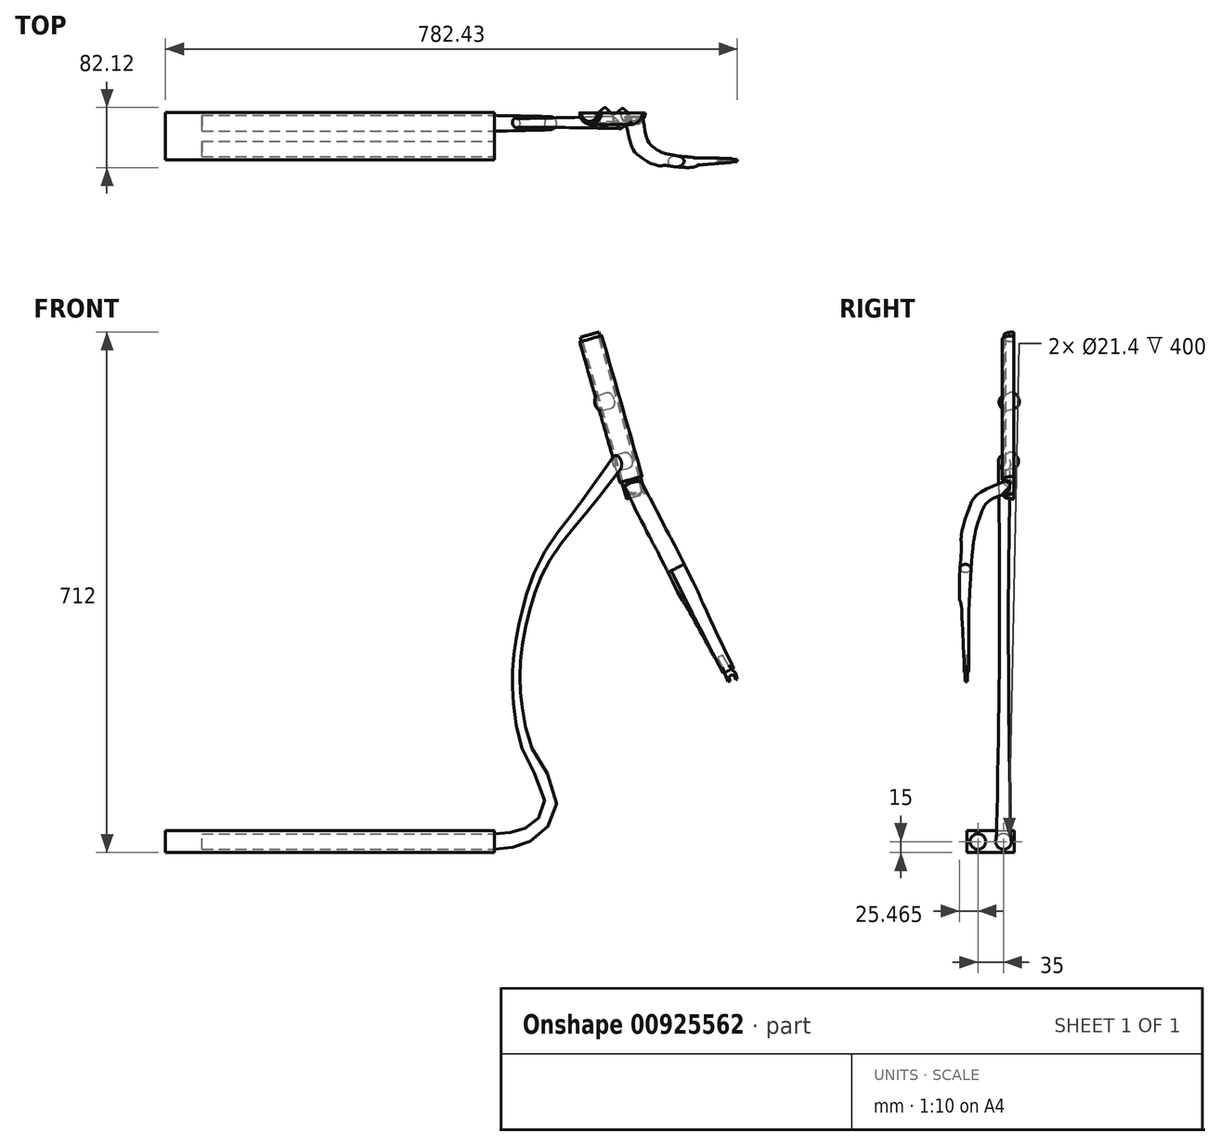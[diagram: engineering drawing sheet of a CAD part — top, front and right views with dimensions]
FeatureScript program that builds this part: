
annotation { "Feature Type Name" : "Feature", "Feature Type Description" : "" }
export const myFeature = defineFeature(function(context is Context, id is Id, definition is map)
    precondition{}
    {
        {
            var Q0;
            Q0=qCreatedBy(makeId("Front.planeOp"),FACE);
            var sketch = newSketch(context, id + "F0", { "sketchPlane" : qUnion([Q0])});
            skLineSegment(sketch, "E0", {"start": v(-867.72, 25) * mm, "end": v(859.87, 25) * mm, "construction": true});
            skLineSegment(sketch, "E1", {"start": v(-316.45, 130) * mm, "end": v(506.8, 130) * mm, "construction": true});
            skLineSegment(sketch, "E2", {"start": v(553.9, -69.15) * mm, "end": v(287, 861.66) * mm, "construction": true});
            skLineSegment(sketch, "E3", {"start": v(-370.15, 525) * mm, "end": v(884.43, 525) * mm, "construction": true});
            skCircle(sketch, "E4", {"center": v(508.78, 298.91) * mm, "radius": 250 * mm, "construction": true});
            skLineSegment(sketch, "E5", {"start": v(508.78, 298.91) * mm, "end": v(455.91, 283.75) * mm, "construction": true});
            skLineSegment(sketch, "E6", {"start": v(508.78, 298.91) * mm, "end": v(371.65, 566.47) * mm, "construction": true});
            skLineSegment(sketch, "E7", {"start": v(-351.72, 690) * mm, "end": v(523.86, 690) * mm, "construction": true});
            skPoint(sketch, "E8", {"position": v(339.42, 690) * mm});
            skLineSegment(sketch, "E9", {"start": v(359.58, 571.29) * mm, "end": v(395.31, 584.53) * mm});
            skLineSegment(sketch, "E10", {"start": v(306.42, 764.88) * mm, "end": v(341.25, 777.78) * mm});
            skCircle(sketch, "E11", {"center": v(-491.22, 301.56) * mm, "radius": 250 * mm, "construction": true});
            skLineSegment(sketch, "E12", {"start": v(-491.22, 301.56) * mm, "end": v(831.47, 298.91) * mm, "construction": true});
            skLineSegment(sketch, "E13.bottom", {"start": v(225, 111.68) * mm, "end": v(-225, 111.68) * mm, "construction": true});
            skLineSegment(sketch, "E13.top", {"start": v(225, -11.68) * mm, "end": v(-225, -11.68) * mm, "construction": true});
            skLineSegment(sketch, "E13.left", {"start": v(225, 111.68) * mm, "end": v(225, -11.68) * mm, "construction": true});
            skLineSegment(sketch, "E13.right", {"start": v(-225, 111.68) * mm, "end": v(-225, -11.68) * mm, "construction": true});
            skPoint(sketch, "E13.middle", {"position": v(0, 50) * mm});
            skLineSegment(sketch, "E14", {"start": v(-491.22, 301.56) * mm, "end": v(-225, 111.68) * mm, "construction": true});
            skLineSegment(sketch, "E15", {"start": v(225, 111.68) * mm, "end": v(220.1, 287.85) * mm, "construction": true});
            skCircle(sketch, "E16", {"center": v(508.78, 298.91) * mm, "radius": 275 * mm});
            skCircle(sketch, "E17", {"center": v(-491.22, 301.56) * mm, "radius": 275 * mm});
            skArc(sketch, "E18", {"start": v(359.58, 571.29) * mm, "mid": v(254.76, 446.83) * mm, "end": v(220.1, 287.85) * mm, "construction": true});
            skSolve(sketch);
        }
        {
            var Q0;
            Q0=qCreatedBy(makeId("Front.planeOp"),FACE);
            var sketch = newSketch(context, id + "F1", { "sketchPlane" : qUnion([Q0])});
            skLineSegment(sketch, "E19", {"start": v(363.24, 558.02) * mm, "end": v(546.56, 610.6) * mm, "construction": true});
            skSolve(sketch);
        }
        {
            var Q0;
            Q0=sQuery(id+"F1.wireOp",EDGE,"E19");
            cPlane(context, id + "F2", {"entities" : qUnion([Q0]), "cplaneType" : CPlaneType.LINE_ANGLE, "offset" : 25 * mm, "angle" : 90 * degree, "width" : 150 * mm, "height" : 150 * mm});
        }
        {
            var Q0;
            Q0=qCreatedBy(id+"F2.planeOp",FACE);
            cPlane(context, id + "F3", {"entities" : qUnion([Q0]), "cplaneType" : CPlaneType.OFFSET, "offset" : 200 * mm, "width" : 150 * mm, "height" : 150 * mm});
        }
        {
            var Q0;
            Q0=qCreatedBy(id+"F2.planeOp",FACE);
            var sketch = newSketch(context, id + "F4", { "sketchPlane" : qUnion([Q0])});
            skCircle(sketch, "E20", {"center": v(502.98, 0) * mm, "radius": 19.15 * mm});
            skSolve(sketch);
        }
        {
            var Q0;
            Q0=qCreatedBy(makeId("Front.planeOp"),FACE);
            var sketch = newSketch(context, id + "F5", { "sketchPlane" : qUnion([Q0])});
            skLineSegment(sketch, "E21", {"start": v(330.52, 767.06) * mm, "end": v(385.68, 574.81) * mm});
            skLineSegment(sketch, "E22.0", {"start": v(329.45, 766.44) * mm, "end": v(384.44, 574.77) * mm});
            skLineSegment(sketch, "E23", {"start": v(329.96, 766.9) * mm, "end": v(330.52, 767.06) * mm});
            skLineSegment(sketch, "E24", {"start": v(385.68, 574.81) * mm, "end": v(385.1, 574.65) * mm});
            skPoint(sketch, "E25.visualSharp", {"position": v(336.55, 759.96) * mm});
            skArc(sketch, "E25.filletArc", {"start": v(336.56, 759.92) * mm, "mid": v(336.54, 759.94) * mm, "end": v(336.51, 759.94) * mm});
            skArc(sketch, "E26.filletArc", {"start": v(382.18, 607.52) * mm, "mid": v(382.2, 607.54) * mm, "end": v(382.2, 607.57) * mm});
            skLineSegment(sketch, "E27", {"start": v(329.45, 766.44) * mm, "end": v(330.05, 766.6) * mm});
            skLineSegment(sketch, "E28", {"start": v(330.05, 766.6) * mm, "end": v(329.96, 766.9) * mm});
            skPoint(sketch, "E29.orphan", {"position": v(335.4, 759.62) * mm});
            skLineSegment(sketch, "E30", {"start": v(384.44, 574.77) * mm, "end": v(385.08, 574.95) * mm});
            skLineSegment(sketch, "E31", {"start": v(385, 574.93) * mm, "end": v(385.1, 574.65) * mm});
            skLineSegment(sketch, "E32", {"start": v(326.59, 772) * mm, "end": v(390, 550.9) * mm});
            skLineSegment(sketch, "E33", {"start": v(390, 550.9) * mm, "end": v(388.16, 550.38) * mm});
            skLineSegment(sketch, "E34", {"start": v(388.16, 550.38) * mm, "end": v(324.75, 771.52) * mm});
            skLineSegment(sketch, "E35", {"start": v(324.75, 771.52) * mm, "end": v(326.59, 772) * mm});
            skSolve(sketch);
        }
        {
            var Q0;
            Q0 = qSketchRegion(id + "F5", true);
            var Q1;
            Q1=sQuery(id+"F0.wireOp",EDGE,"E2");
            revolve(context, id + "F6", {"surfaceOperationType" : NewSurfaceOperationType.NEW, "entities" : qUnion([Q0]), "axis" : qUnion([Q1]), "revolveType" : RevolveType.ONE_DIRECTION, "oppositeDirection" : true, "angle" : 180 * degree});
        }
        {
            var Q0;
            Q0=sQuery(id+"F0.wireOp",EDGE,"E6");
            cPlane(context, id + "F7", {"entities" : qUnion([Q0]), "cplaneType" : CPlaneType.LINE_ANGLE, "offset" : 25 * mm, "angle" : 0 * degree, "width" : 150 * mm, "height" : 150 * mm});
        }
        {
            var Q0;
            Q0=qCreatedBy(id+"F7.planeOp",FACE);
            var sketch = newSketch(context, id + "F8", { "sketchPlane" : qUnion([Q0])});
            skLineSegment(sketch, "E36", {"start": v(0, 33.94) * mm, "end": v(-65, 33.94) * mm, "construction": true});
            skFitSpline(sketch, "E37", {"points": [v(-5.34, 328.4) * mm, v(-52.14, 293.61) * mm, v(-62.93, 251.7) * mm, v(-67.18, 151.52) * mm, v(-65, 44.96) * mm], "startDerivative": vector(-442.33, 23.28) * mm, "endDerivative": vector(3.64, -561.75) * mm});
            skSolve(sketch);
        }
        {
            var Q0;
            Q0=sQuery(id+"F8.wireOp",EDGE,"E36");
            var Q1;
            Q1=sQuery(id+"F8.wireOp",VERTEX,"E36.end");
            cPlane(context, id + "F9", {"entities" : qUnion([Q0, Q1]), "cplaneType" : CPlaneType.CURVE_POINT, "offset" : 25 * mm, "width" : 150 * mm, "height" : 150 * mm});
        }
        {
            var Q0;
            Q0=qCreatedBy(id+"F9.planeOp",FACE);
            var sketch = newSketch(context, id + "F10", { "sketchPlane" : qUnion([Q0])});
            skArc(sketch, "E38.0", {"start": v(512.63, 300.02) * mm, "mid": v(507.68, 302.76) * mm, "end": v(504.94, 297.81) * mm});
            skLineSegment(sketch, "E39.0", {"start": v(505.96, 294.61) * mm, "end": v(504.94, 297.81) * mm});
            skLineSegment(sketch, "E40.0", {"start": v(512.63, 300.02) * mm, "end": v(513.62, 296.52) * mm});
            skLineSegment(sketch, "E41", {"start": v(513.62, 296.52) * mm, "end": v(516, 297.2) * mm});
            skLineSegment(sketch, "E42", {"start": v(516, 297.2) * mm, "end": v(513.62, 304.94) * mm});
            skLineSegment(sketch, "E43", {"start": v(505.96, 294.61) * mm, "end": v(503.18, 293.72) * mm});
            skLineSegment(sketch, "E44", {"start": v(503.18, 293.72) * mm, "end": v(501.9, 297.7) * mm});
            skLineSegment(sketch, "E45", {"start": v(501.9, 297.7) * mm, "end": v(495.51, 313.34) * mm});
            skLineSegment(sketch, "E46", {"start": v(503.46, 316.2) * mm, "end": v(513.62, 304.94) * mm});
            skLineSegment(sketch, "E47", {"start": v(503.46, 316.2) * mm, "end": v(495.95, 329.85) * mm});
            skLineSegment(sketch, "E48", {"start": v(495.95, 329.85) * mm, "end": v(489.19, 326.8) * mm});
            skLineSegment(sketch, "E49", {"start": v(489.19, 326.8) * mm, "end": v(495.51, 313.34) * mm});
            skSolve(sketch);
        }
        {
            var Q0;
            Q0 = qSketchRegion(id + "F10", true);
            extrude(context, id + "F11", {"entities" : qUnion([Q0]), "endBound" : BoundingType.SYMMETRIC, "depth" : 3 * mm, "offsetDistance" : 25 * mm});
        }
        {
            var Q0;
            Q0=sQuery(id+"F8.wireOp",EDGE,"E37");
            var Q1;
            Q1=sQuery(id+"F8.wireOp",VERTEX,"E37.end");
            cPlane(context, id + "F12", {"entities" : qUnion([Q0, Q1]), "cplaneType" : CPlaneType.CURVE_POINT, "offset" : 25 * mm, "width" : 150 * mm, "height" : 150 * mm});
        }
        {
            var Q0;
            Q0=qCreatedBy(id+"F12.planeOp",FACE);
            var sketch = newSketch(context, id + "F13", { "sketchPlane" : qUnion([Q0])});
            skEllipse(sketch, "E50", {"center": v(589.33, 62.75) * mm, "majorRadius": 8 * mm, "minorRadius": 3 * mm, "majorAxis": v(-1, 0)});
            skSolve(sketch);
        }
        {
            var Q0;
            Q0=sQuery(id+"F8.wireOp",VERTEX,"E37.3.internal");
            var Q1;
            Q1=sQuery(id+"F8.wireOp",EDGE,"E37");
            cPlane(context, id + "F14", {"entities" : qUnion([Q0, Q1]), "cplaneType" : CPlaneType.CURVE_POINT, "offset" : 25 * mm, "width" : 150 * mm, "height" : 150 * mm});
        }
        {
            var Q0;
            Q0=sQuery(id+"F8.wireOp",EDGE,"E37");
            cPoint(context, id + "F15", {"entities" : qUnion([Q0]), "parameter" : 0.5});
        }
        {
            var Q0;
            Q0 = qCreatedBy(id + "F15" ,VERTEX);
            var Q1;
            Q1=sQuery(id+"F8.wireOp",EDGE,"E37");
            cPlane(context, id + "F16", {"entities" : qUnion([Q0, Q1]), "cplaneType" : CPlaneType.CURVE_POINT, "offset" : 25 * mm, "width" : 150 * mm, "height" : 150 * mm});
        }
        {
            var Q0;
            Q0=qCreatedBy(id+"F16.planeOp",FACE);
            var sketch = newSketch(context, id + "F17", { "sketchPlane" : qUnion([Q0])});
            skEllipse(sketch, "E51", {"center": v(587.69, 84.2) * mm, "majorRadius": 12.5 * mm, "minorRadius": 7.5 * mm, "majorAxis": v(-1, 0)});
            skSolve(sketch);
        }
        {
            var Q0;
            Q0=sQuery(id+"F8.wireOp",VERTEX,"E37.2.internal");
            var Q1;
            Q1=sQuery(id+"F8.wireOp",EDGE,"E37");
            cPlane(context, id + "F18", {"entities" : qUnion([Q0, Q1]), "cplaneType" : CPlaneType.CURVE_POINT, "offset" : 25 * mm, "width" : 150 * mm, "height" : 150 * mm});
        }
        {
            var Q0;
            Q0=qCreatedBy(id+"F18.planeOp",FACE);
            var sketch = newSketch(context, id + "F19", { "sketchPlane" : qUnion([Q0])});
            skEllipse(sketch, "E52", {"center": v(581.49, 134.07) * mm, "majorRadius": 12.5 * mm, "minorRadius": 9 * mm, "majorAxis": v(-1, 0)});
            skSolve(sketch);
        }
        {
            var Q0;
            Q0=sQuery(id+"F8.wireOp",VERTEX,"E37.1.internal");
            var Q1;
            Q1=sQuery(id+"F8.wireOp",EDGE,"E37");
            cPlane(context, id + "F20", {"entities" : qUnion([Q0, Q1]), "cplaneType" : CPlaneType.CURVE_POINT, "offset" : 25 * mm, "width" : 150 * mm, "height" : 150 * mm});
        }
        {
            var Q0;
            Q0=qCreatedBy(id+"F20.planeOp",FACE);
            var sketch = newSketch(context, id + "F21", { "sketchPlane" : qUnion([Q0])});
            skEllipse(sketch, "E53", {"center": v(553.64, 251.52) * mm, "majorRadius": 12.5 * mm, "minorRadius": 9 * mm, "majorAxis": v(-1, 0)});
            skSolve(sketch);
        }
        {
            var Q0;
            Q0=sQuery(id+"F8.wireOp",VERTEX,"E37.start");
            var Q1;
            Q1=sQuery(id+"F8.wireOp",EDGE,"E37");
            cPlane(context, id + "F22", {"entities" : qUnion([Q0, Q1]), "cplaneType" : CPlaneType.CURVE_POINT, "offset" : 25 * mm, "width" : 150 * mm, "height" : 150 * mm});
        }
        {
            var Q0;
            Q0=qCreatedBy(id+"F22.planeOp",FACE);
            var sketch = newSketch(context, id + "F23", { "sketchPlane" : qUnion([Q0])});
            skEllipse(sketch, "E54", {"center": v(374.92, 560.35) * mm, "majorRadius": 12.5 * mm, "minorRadius": 9 * mm, "majorAxis": v(-1, 0)});
            skSolve(sketch);
        }
        {
            var Q0;
            Q0=sQuery(id+"F8.wireOp",EDGE,"E37");
            var Q2;
            Q2=makeQuery(id+"F13.imprint","IMPRINT",FACE,{"disambiguationData":[TD([[makeQuery(id+"F13.imprint","IMPRINT",EDGE,{"derivedFrom":sQuery(id+"F13.wireOp",EDGE,"E50")}),1.0]])]});
            var Q3;
            Q3=makeQuery(id+"F17.imprint","IMPRINT",FACE,{"disambiguationData":[TD([[makeQuery(id+"F17.imprint","IMPRINT",EDGE,{"derivedFrom":sQuery(id+"F17.wireOp",EDGE,"E51")}),1.0]])]});
            var Q4;
            Q4=makeQuery(id+"F19.imprint","IMPRINT",FACE,{"disambiguationData":[TD([[makeQuery(id+"F19.imprint","IMPRINT",EDGE,{"derivedFrom":sQuery(id+"F19.wireOp",EDGE,"E52")}),1.0]])]});
            var Q5;
            Q5=makeQuery(id+"F21.imprint","IMPRINT",FACE,{"disambiguationData":[TD([[makeQuery(id+"F21.imprint","IMPRINT",EDGE,{"derivedFrom":sQuery(id+"F21.wireOp",EDGE,"E53")}),1.0]])]});
            var Q6;
            Q6=makeQuery(id+"F23.imprint","IMPRINT",FACE,{"disambiguationData":[TD([[makeQuery(id+"F23.imprint","IMPRINT",EDGE,{"derivedFrom":sQuery(id+"F23.wireOp",EDGE,"E54")}),1.0]])]});
            loft(context, id + "F24", {"addSections" : true, "spine" : qUnion([Q0]), "sectionCount" : 5, "sheetProfilesArray" : [{ "sheetProfileEntities" : qUnion([Q2]) }, { "sheetProfileEntities" : qUnion([Q3]) }, { "sheetProfileEntities" : qUnion([Q4]) }, { "sheetProfileEntities" : qUnion([Q5]) }, { "sheetProfileEntities" : qUnion([Q6]) }]});
        }
        {
            var Q0;
            Q0=makeQuery(id+"F24.opLoft","SWEPT_BODY",BODY,{"disambiguationData":[OSD([makeQuery(id+"F13.imprint","IMPRINT",FACE,{"disambiguationData":[TD([[makeQuery(id+"F13.imprint","IMPRINT",EDGE,{"derivedFrom":sQuery(id+"F13.wireOp",EDGE,"E50")}),1.0]])]}),sQuery(id+"F17.wireOp",EDGE,"E51"),sQuery(id+"F19.wireOp",EDGE,"E52"),sQuery(id+"F21.wireOp",EDGE,"E53"),makeQuery(id+"F23.imprint","IMPRINT",FACE,{"disambiguationData":[TD([[makeQuery(id+"F23.imprint","IMPRINT",EDGE,{"derivedFrom":sQuery(id+"F23.wireOp",EDGE,"E54")}),1.0]])]})])]});
            var Q1;
            Q1=makeQuery(id+"F6.opRevolve","SWEPT_BODY",BODY,{"disambiguationData":[OSD([sQuery(id+"F5.wireOp",EDGE,"E32"),sQuery(id+"F5.wireOp",EDGE,"E33"),sQuery(id+"F5.wireOp",EDGE,"E34"),sQuery(id+"F5.wireOp",EDGE,"E35")])]});
            booleanBodies(context, id + "F25", {"operationType" : BooleanOperationType.UNION, "tools" : qUnion([Q0, Q1])});
        }
        {
            var Q0;
            Q0=makeQuery(id+"F25.opBoolean","INTERSECT",EDGE,{"derivedFrom":[makeQuery(id+"F6.opRevolve","SWEPT_FACE",FACE,{"disambiguationData":[OSD([sQuery(id+"F5.wireOp",EDGE,"E32")])]}),makeQuery(id+"F24.opLoft","SWEPT_FACE",FACE,{"disambiguationData":[OSD([sQuery(id+"F13.wireOp",EDGE,"E50"),sQuery(id+"F17.wireOp",EDGE,"E51"),sQuery(id+"F19.wireOp",EDGE,"E52"),sQuery(id+"F21.wireOp",EDGE,"E53"),sQuery(id+"F23.wireOp",EDGE,"E54")])]})]});
            fillet(context, id + "F26", {"entities" : qUnion([Q0]), "radius" : 2 * mm, "tangentPropagation" : true, "allowEdgeOverflow" : false});
        }
        {
            var Q0;
            Q0=qCreatedBy(makeId("Top.planeOp"),FACE);
            var sketch = newSketch(context, id + "F27", { "sketchPlane" : qUnion([Q0])});
            skLineSegment(sketch, "E55", {"start": v(563.3, -65) * mm, "end": v(-532.03, -65) * mm, "construction": true});
            skLineSegment(sketch, "E56", {"start": v(532.67, 0) * mm, "end": v(432.3, -70.28) * mm, "construction": true});
            skLineSegment(sketch, "E57.0", {"start": v(553.9, 0) * mm, "end": v(287, 0) * mm, "construction": true});
            skLineSegment(sketch, "E58", {"start": v(258, 0) * mm, "end": v(258, -65) * mm, "construction": true});
            skLineSegment(sketch, "E59", {"start": v(-116.26, 0) * mm, "end": v(-116.26, -65) * mm, "construction": true});
            skSolve(sketch);
        }
        {
            var Q0;
            Q0=qCreatedBy(makeId("Top.planeOp"),FACE);
            cPlane(context, id + "F28", {"entities" : qUnion([Q0]), "cplaneType" : CPlaneType.OFFSET, "offset" : 60 * mm, "width" : 150 * mm, "height" : 150 * mm});
        }
        {
            var Q0;
            Q0=qCreatedBy(id+"F28.planeOp",FACE);
            var sketch = newSketch(context, id + "F29", { "sketchPlane" : qUnion([Q0])});
            skLineSegment(sketch, "E60.bottom", {"start": v(-266.42, -64.23) * mm, "end": v(183.58, -64.23) * mm});
            skLineSegment(sketch, "E60.top", {"start": v(-266.42, 0.77) * mm, "end": v(183.58, 0.77) * mm});
            skLineSegment(sketch, "E60.left", {"start": v(-266.42, -64.23) * mm, "end": v(-266.42, 0.77) * mm});
            skLineSegment(sketch, "E60.right", {"start": v(183.58, -64.23) * mm, "end": v(183.58, 0.77) * mm});
            skLineSegment(sketch, "E61", {"start": v(147.84, -52.31) * mm, "end": v(218.13, -52.31) * mm, "construction": true});
            skSolve(sketch);
        }
        {
            var Q0;
            Q0 = qSketchRegion(id + "F29", true);
            extrude(context, id + "F30", {"entities" : qUnion([Q0]), "depth" : 30 * mm, "offsetDistance" : 25 * mm});
        }
        {
            var Q0;
            Q0=sQuery(id+"F0.wireOp",VERTEX,"E8");
            var Q1;
            Q1=sQuery(id+"F27.wireOp",VERTEX,"E56.start");
            var Q2;
            Q2=sQuery(id+"F27.wireOp",VERTEX,"E56.end");
            cPlane(context, id + "F31", {"entities" : qUnion([Q0, Q1, Q2]), "cplaneType" : CPlaneType.THREE_POINT, "offset" : 25 * mm, "width" : 150 * mm, "height" : 150 * mm});
        }
        {
            var Q0;
            Q0=makeQuery(id+"F30.opExtrude","SWEPT_FACE",FACE,{"disambiguationData":[OSD([sQuery(id+"F29.wireOp",EDGE,"E60.right")])]});
            var sketch = newSketch(context, id + "F32", { "sketchPlane" : qUnion([Q0])});
            skLineSegment(sketch, "E62", {"start": v(-64.23, 75) * mm, "end": v(0.77, 75) * mm, "construction": true});
            skCircle(sketch, "E63", {"center": v(-49.23, 75) * mm, "radius": 12.5 * mm});
            skCircle(sketch, "E64.0", {"center": v(-49.23, 75) * mm, "radius": 10.7 * mm});
            skCircle(sketch, "E65", {"center": v(-14.23, 75) * mm, "radius": 12.5 * mm});
            skCircle(sketch, "E66.0", {"center": v(-14.23, 75) * mm, "radius": 10.7 * mm});
            skSolve(sketch);
        }
        {
            var Q0;
            Q0=makeQuery(id+"F32.imprint","IMPRINT",FACE,{"disambiguationData":[TD([[makeQuery(id+"F32.imprint","IMPRINT",EDGE,{"derivedFrom":sQuery(id+"F32.wireOp",EDGE,"E64.0")}),1.0]])]});
            var Q1;
            Q1=makeQuery(id+"F32.imprint","IMPRINT",FACE,{"disambiguationData":[TD([[makeQuery(id+"F32.imprint","IMPRINT",EDGE,{"derivedFrom":sQuery(id+"F32.wireOp",EDGE,"E66.0")}),1.0]])]});
            extrude(context, id + "F33", {"entities" : qUnion([Q0, Q1]), "operationType" : NewBodyOperationType.REMOVE, "oppositeDirection" : true, "depth" : 400 * mm, "offsetDistance" : 25 * mm});
        }
        {
            var Q0;
            Q0=sQuery(id+"F32.wireOp",EDGE,"E62");
            cPlane(context, id + "F34", {"entities" : qUnion([Q0]), "cplaneType" : CPlaneType.LINE_ANGLE, "offset" : 25 * mm, "angle" : 0 * degree, "width" : 150 * mm, "height" : 150 * mm});
        }
        {
            var Q0;
            Q0=qCreatedBy(id+"F34.planeOp",FACE);
            var sketch = newSketch(context, id + "F35", { "sketchPlane" : qUnion([Q0])});
            skLineSegment(sketch, "E67", {"start": v(129.45, -49.23) * mm, "end": v(331.95, -49.23) * mm, "construction": true});
            skSolve(sketch);
        }
        {
            var Q0;
            Q0=qCreatedBy(id+"F31.planeOp",FACE);
            var Q1;
            Q1=sQuery(id+"F0.wireOp",EDGE,"E2");
            cPlane(context, id + "F36", {"entities" : qUnion([Q0, Q1]), "cplaneType" : CPlaneType.LINE_ANGLE, "offset" : 25 * mm, "angle" : 90 * degree, "width" : 150 * mm, "height" : 150 * mm});
        }
        {
            var Q0;
            Q0=qCreatedBy(id+"F36.planeOp",FACE);
            cPlane(context, id + "F37", {"entities" : qUnion([Q0]), "cplaneType" : CPlaneType.OFFSET, "offset" : 25 * mm, "width" : 150 * mm, "height" : 150 * mm});
        }
        {
            var Q0;
            Q0=qCreatedBy(id+"F37.planeOp",FACE);
            var sketch = newSketch(context, id + "F38", { "sketchPlane" : qUnion([Q0])});
            skEllipse(sketch, "E68", {"center": v(309.8, 559.66) * mm, "majorRadius": 11.25 * mm, "minorRadius": 11.25 * mm, "majorAxis": v(0, -1)});
            skEllipse(sketch, "E69", {"center": v(311.17, 474.46) * mm, "majorRadius": 11.25 * mm, "minorRadius": 11.25 * mm, "majorAxis": v(0, -1)});
            skSolve(sketch);
        }
        {
            var Q0;
            Q0=qCreatedBy(id+"F36.planeOp",FACE);
            var sketch = newSketch(context, id + "F39", { "sketchPlane" : qUnion([Q0])});
            skEllipse(sketch, "E70", {"center": v(303.97, 558.29) * mm, "majorRadius": 11.25 * mm, "minorRadius": 11.25 * mm, "majorAxis": v(0, -1)});
            skEllipse(sketch, "E71", {"center": v(305.34, 473.09) * mm, "majorRadius": 11.25 * mm, "minorRadius": 11.25 * mm, "majorAxis": v(0, -1)});
            skSolve(sketch);
        }
        {
            var Q0;
            Q0 = qSketchRegion(id + "F39", true);
            extrude(context, id + "F40", {"entities" : qUnion([Q0]), "depth" : 17.5 * mm, "offsetDistance" : 25 * mm, "hasDraft" : true, "draftAngle" : 3 * degree, "draftPullDirection" : true});
        }
        {
            var Q0;
            Q0=makeQuery(id+"F40.opExtrude","SWEPT_FACE",FACE,{"disambiguationData":[OSD([sQuery(id+"F39.wireOp",EDGE,"E71")])]});
            var Q1;
            Q1=makeQuery(id+"F6.opRevolve","SWEPT_FACE",FACE,{"disambiguationData":[OSD([sQuery(id+"F5.wireOp",EDGE,"E21")])]});
            var Q2;
            Q2=makeQuery(id+"F40.opExtrude","SWEPT_FACE",FACE,{"disambiguationData":[OSD([sQuery(id+"F39.wireOp",EDGE,"E70")])]});
            fillet(context, id + "F41", {"entities" : qUnion([Q0, Q1, Q2]), "radius" : 0.03 * mm, "tangentPropagation" : true, "allowEdgeOverflow" : false});
        }
        {
            var Q0;
            Q0=makeQuery(id+"F40.opExtrude","CAP_FACE",FACE,{"disambiguationData":[OSD([sQuery(id+"F39.wireOp",EDGE,"E71")])],"isStart":false});
            var sketch = newSketch(context, id + "F42", { "sketchPlane" : qUnion([Q0])});
            skPoint(sketch, "E72", {"position": v(306.56, 473.18) * mm});
            skSolve(sketch);
        }
        {
            var Q0;
            Q0=qCreatedBy(id+"F34.planeOp",FACE);
            var sketch = newSketch(context, id + "F43", { "sketchPlane" : qUnion([Q0])});
            skLineSegment(sketch, "E73", {"start": v(129.42, -14.23) * mm, "end": v(260.82, -14.23) * mm, "construction": true});
            skSolve(sketch);
        }
        {
            var Q0;
            Q0=sQuery(id+"F43.wireOp",VERTEX,"E73.start");
            var Q1;
            Q1=sQuery(id+"F43.wireOp",VERTEX,"E73.end");
            var Q2;
            Q2=sQuery(id+"F42.wireOp",VERTEX,"E72");
            cPlane(context, id + "F44", {"entities" : qUnion([Q0, Q1, Q2]), "cplaneType" : CPlaneType.THREE_POINT, "offset" : 25 * mm, "width" : 150 * mm, "height" : 150 * mm});
        }
        {
            var Q0;
            Q0=qCreatedBy(id+"F44.planeOp",FACE);
            var sketch = newSketch(context, id + "F45", { "sketchPlane" : qUnion([Q0])});
            skFitSpline(sketch, "E74", {"points": [v(-356.71, 602.91) * mm, v(-313.14, 544.57) * mm, v(-265.3, 483) * mm, v(-237.18, 429.96) * mm, v(-218.35, 360.74) * mm, v(-213.23, 320.56) * mm, v(-214.93, 258.17) * mm, v(-239.37, 176.29) * mm, v(-258.9, 143.47) * mm, v(-245.62, 95.02) * mm, v(-183.58, 75) * mm], "startDerivative": vector(774.68, -968.54) * mm, "endDerivative": vector(439.55, -6.28) * mm});
            skSolve(sketch);
        }
        {
            var Q0;
            Q0=sQuery(id+"F45.wireOp",EDGE,"E74");
            var Q1;
            {var subQ0=sQuery(id+"F39.wireOp",EDGE,"E71");Q1=makeQuery(id+"F42.imprint","IMPRINT",FACE,{"disambiguationData":[TD([[makeQuery(id+"F42.imprint","IMPRINT",EDGE,{"derivedFrom":makeQuery(id+"F41.opFillet","BLEND_EDGE",EDGE,{"blendedFrom":[makeQuery(id+"F40.opExtrude","CAP_EDGE",EDGE,{"disambiguationData":[OSD([subQ0])],"isStart":false}),makeQuery(id+"F40.opExtrude","CAP_FACE",FACE,{"disambiguationData":[OSD([subQ0])],"isStart":false})],"blendedInto":[makeQuery(id+"F40.opExtrude","CAP_FACE",FACE,{"disambiguationData":[OSD([subQ0])],"isStart":false})]})}),1.0]])]});}
            var Q2;
            Q2=makeQuery(id+"F32.imprint","IMPRINT",FACE,{"disambiguationData":[TD([[makeQuery(id+"F32.imprint","IMPRINT",EDGE,{"derivedFrom":sQuery(id+"F32.wireOp",EDGE,"E66.0")}),1.0]])]});
            loft(context, id + "F46", {"addSections" : true, "spine" : qUnion([Q0]), "sectionCount" : 12, "sheetProfilesArray" : [{ "sheetProfileEntities" : qUnion([Q1]) }, { "sheetProfileEntities" : qUnion([Q2]) }]});
        }
    });
